# Revit family: Bathtub-Freestanding-DXV-Modulus-D12031000.415
name_source: partatom
category: Plumbing Fixtures
units: mm (PartAtom-declared; Revit-internal decimal feet)

## family parameters
Always vertical = No
Cut with Voids When Loaded = No
OmniClass Number = 23.45.05.14.21
OmniClass Title = Bathtubs
Part Type = Normal
Room Calculation Point = No
Round Connector Dimension = Use Radius
Shared = Yes
Work Plane-Based = Yes

## types (3) — shared parameters
Assembly Code = D2010510
CSA B45.5/IAPMO Z124 = Yes
CW Connection = No
CWFU = 5
Default Elevation = 0"
Description = DXV Modulus™ Freestanding Soaking Tub
Finish = Acrylic-DXV-415-Canvas White
HW Connection = No
Height = 24"
Installation Instruction Link = https://dxv01.blob.core.windows.net
Installation Type = Floor Mounted
Length = 32"
Manufacturer = DXV
Material = Acrylic-DXV-415-Canvas White
Price = Prices may vary. Please consult manufacturer representative for most up to date price list.
Product Documentation Link = https://dxv01.blob.core.windows.net
Product Page URL = https://www.dxv.com
Revised Date = 03/07/2022
Shipping Weight = 121 lbs (54.9 kg)
Tub Capacity = 81 gallon (307 L.) capacity
URL = www.dxv.com
Vent Connection = No
WFU = 5
Waste Connection = Yes
Width = 72"
zero-valued in all types: HWFU

## per-type parameters (varying)
| type | 755491-201-0080A Drain Cap & Plug-Polished Nickel (008) | 755491-201-2950A Drain Cap & Plug-Brushed Nickel (295) | 755491-201.2430A Drain Cap & Plug-Matte Black (243) | Drain Finish | Drain Material | Waste Connection Diameter | Waste Connection Radius |
| D12031000.415 w/ 755491-201-0080A | Yes | No | No | Metal-DXV-008-Polished Nickel | Metal-DXV-008-Polished Nickel | 3" | 1 1/2" |
| D12031000.415 w/ 755491-201-2430A | No | No | Yes | Metal-DXV-243-Matte Black | Metal-DXV-243-Matte Black | 1 1/2" | 1" |
| D12031000.415 w/ 755491-201-2950A | No | Yes | No | Metal-DXV-295-Brushed Chrome | Metal-DXV-295-Brushed Chrome | 3" | 1 1/2" |

note: column(s) folded — value = type name in every type: Model

## geometry (parser evidence)
native form markers: Sweep x2
no freeform markers — native parametric forms only
